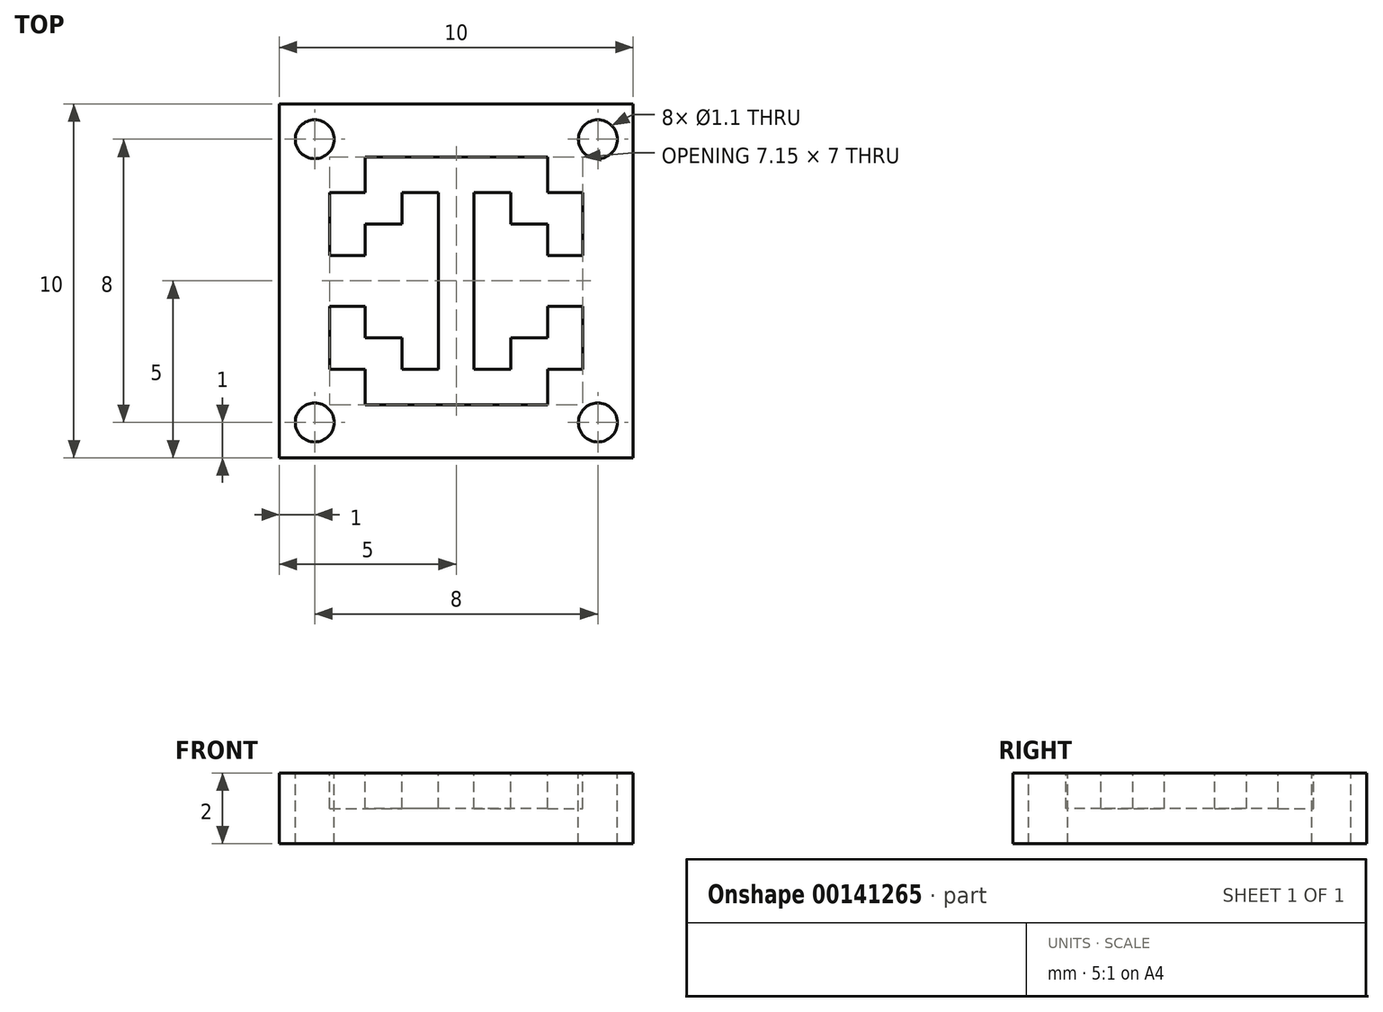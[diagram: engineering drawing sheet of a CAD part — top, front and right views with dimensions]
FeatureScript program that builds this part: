
annotation { "Feature Type Name" : "Feature", "Feature Type Description" : "" }
export const myFeature = defineFeature(function(context is Context, id is Id, definition is map)
    precondition{}
    {
        {
            var Q0;
            Q0=qCreatedBy(makeId("Top.planeOp"),FACE);
            var sketch = newSketch(context, id + "F0", { "sketchPlane" : qUnion([Q0])});
            skLineSegment(sketch, "E0.bottom", {"start": v(5, 5) * mm, "end": v(-5, 5) * mm});
            skLineSegment(sketch, "E0.top", {"start": v(5, -5) * mm, "end": v(-5, -5) * mm});
            skLineSegment(sketch, "E0.left", {"start": v(5, 5) * mm, "end": v(5, -5) * mm});
            skLineSegment(sketch, "E0.right", {"start": v(-5, 5) * mm, "end": v(-5, -5) * mm});
            skLineSegment(sketch, "E1.left", {"start": v(0.5, 0.5) * mm, "end": v(0.5, -0.5) * mm});
            skLineSegment(sketch, "E2", {"start": v(-0.5, 0.5) * mm, "end": v(-0.5, -0.5) * mm});
            skLineSegment(sketch, "E3", {"start": v(-0.5, -0.5) * mm, "end": v(-0.5, -2.5) * mm});
            skLineSegment(sketch, "E4", {"start": v(0.5, -0.5) * mm, "end": v(0.5, -2.5) * mm});
            skLineSegment(sketch, "E5", {"start": v(-0.5, -3.5) * mm, "end": v(-2.58, -3.5) * mm});
            skLineSegment(sketch, "E6", {"start": v(-0.5, -2.5) * mm, "end": v(-1.54, -2.5) * mm});
            skLineSegment(sketch, "E7", {"start": v(-3.58, -2.5) * mm, "end": v(-3.58, -0.71) * mm});
            skLineSegment(sketch, "E8", {"start": v(-3.58, -0.71) * mm, "end": v(-2.58, -0.71) * mm});
            skLineSegment(sketch, "E9", {"start": v(-2.58, -0.71) * mm, "end": v(-2.58, -1.6) * mm});
            skLineSegment(sketch, "E10", {"start": v(-0.5, -3.5) * mm, "end": v(0.5, -3.5) * mm});
            skLineSegment(sketch, "E11.MirrorCS", {"start": v(-0.5, 3.5) * mm, "end": v(0.5, 3.5) * mm});
            skLineSegment(sketch, "E12.MirrorCS", {"start": v(0.5, 0.5) * mm, "end": v(0.5, 2.5) * mm});
            skLineSegment(sketch, "E13.MirrorCS", {"start": v(-0.5, 0.5) * mm, "end": v(-0.5, 2.5) * mm});
            skLineSegment(sketch, "E14", {"start": v(-5, 0) * mm, "end": v(5, 0) * mm, "construction": true});
            skLineSegment(sketch, "E15", {"start": v(0, 5) * mm, "end": v(0, -5) * mm, "construction": true});
            skPoint(sketch, "E15.endSnap0", {"position": v(0, 5) * mm});
            skCircle(sketch, "E16", {"center": v(-4, -4) * mm, "radius": 0.55 * mm});
            skCircle(sketch, "E17.MirrorC", {"center": v(4, -4) * mm, "radius": 0.55 * mm});
            skCircle(sketch, "E18.MirrorC", {"center": v(-4, 4) * mm, "radius": 0.55 * mm});
            skLineSegment(sketch, "E19", {"start": v(-1.54, -2.5) * mm, "end": v(-1.54, -1.6) * mm});
            skLineSegment(sketch, "E20", {"start": v(-2.58, -1.6) * mm, "end": v(-1.54, -1.6) * mm});
            skLineSegment(sketch, "E21", {"start": v(-2.58, -2.5) * mm, "end": v(-2.58, -3.5) * mm});
            skLineSegment(sketch, "E22", {"start": v(-2.58, -2.5) * mm, "end": v(-3.58, -2.5) * mm});
            skLineSegment(sketch, "E23.MirrorCS", {"start": v(0.5, -3.5) * mm, "end": v(2.58, -3.5) * mm});
            skLineSegment(sketch, "E24.MirrorCS", {"start": v(2.58, -2.5) * mm, "end": v(2.58, -3.5) * mm});
            skLineSegment(sketch, "E25.MirrorCS", {"start": v(2.58, -2.5) * mm, "end": v(3.58, -2.5) * mm});
            skLineSegment(sketch, "E26.MirrorCS", {"start": v(3.58, -2.5) * mm, "end": v(3.58, -0.71) * mm});
            skLineSegment(sketch, "E27.MirrorCS", {"start": v(3.58, -0.71) * mm, "end": v(2.58, -0.71) * mm});
            skLineSegment(sketch, "E28.MirrorCS", {"start": v(2.58, -0.71) * mm, "end": v(2.58, -1.6) * mm});
            skLineSegment(sketch, "E29.MirrorCS", {"start": v(2.58, -1.6) * mm, "end": v(1.54, -1.6) * mm});
            skLineSegment(sketch, "E30.MirrorCS", {"start": v(1.54, -2.5) * mm, "end": v(1.54, -1.6) * mm});
            skLineSegment(sketch, "E31.MirrorCS", {"start": v(0.5, -2.5) * mm, "end": v(1.54, -2.5) * mm});
            skCircle(sketch, "E32.MirrorC", {"center": v(4, 4) * mm, "radius": 0.55 * mm});
            skLineSegment(sketch, "E33.MirrorCS", {"start": v(-0.5, 2.5) * mm, "end": v(-1.54, 2.5) * mm});
            skLineSegment(sketch, "E34.MirrorCS", {"start": v(-1.54, 2.5) * mm, "end": v(-1.54, 1.6) * mm});
            skLineSegment(sketch, "E35.MirrorCS", {"start": v(-2.58, 1.6) * mm, "end": v(-1.54, 1.6) * mm});
            skLineSegment(sketch, "E36.MirrorCS", {"start": v(-2.58, 0.71) * mm, "end": v(-2.58, 1.6) * mm});
            skLineSegment(sketch, "E37.MirrorCS", {"start": v(-3.58, 0.71) * mm, "end": v(-2.58, 0.71) * mm});
            skLineSegment(sketch, "E38.MirrorCS", {"start": v(-3.58, 2.5) * mm, "end": v(-3.58, 0.71) * mm});
            skLineSegment(sketch, "E39.MirrorCS", {"start": v(-2.58, 2.5) * mm, "end": v(-3.58, 2.5) * mm});
            skLineSegment(sketch, "E40.MirrorCS", {"start": v(-2.58, 2.5) * mm, "end": v(-2.58, 3.5) * mm});
            skLineSegment(sketch, "E41.MirrorCS", {"start": v(-0.5, 3.5) * mm, "end": v(-2.58, 3.5) * mm});
            skLineSegment(sketch, "E42.MirrorCS", {"start": v(0.5, 3.5) * mm, "end": v(2.58, 3.5) * mm});
            skLineSegment(sketch, "E43.MirrorCS", {"start": v(2.58, 2.5) * mm, "end": v(2.58, 3.5) * mm});
            skLineSegment(sketch, "E44.MirrorCS", {"start": v(2.58, 2.5) * mm, "end": v(3.58, 2.5) * mm});
            skLineSegment(sketch, "E45.MirrorCS", {"start": v(3.58, 2.5) * mm, "end": v(3.58, 0.71) * mm});
            skLineSegment(sketch, "E46.MirrorCS", {"start": v(3.58, 0.71) * mm, "end": v(2.58, 0.71) * mm});
            skLineSegment(sketch, "E47.MirrorCS", {"start": v(2.58, 0.71) * mm, "end": v(2.58, 1.6) * mm});
            skLineSegment(sketch, "E48.MirrorCS", {"start": v(2.58, 1.6) * mm, "end": v(1.54, 1.6) * mm});
            skLineSegment(sketch, "E49.MirrorCS", {"start": v(1.54, 2.5) * mm, "end": v(1.54, 1.6) * mm});
            skLineSegment(sketch, "E50.MirrorCS", {"start": v(0.5, 2.5) * mm, "end": v(1.54, 2.5) * mm});
            skSolve(sketch);
        }
        {
            var Q0;
            Q0=makeQuery(id+"F0.imprint","IMPRINT",FACE,{"disambiguationData":[TD([[makeQuery(id+"F0.imprint","IMPRINT",EDGE,{"derivedFrom":sQuery(id+"F0.wireOp",EDGE,"E0.bottom")}),1.0]])]});
            var Q1;
            Q1=makeQuery(id+"F0.imprint","IMPRINT",FACE,{"disambiguationData":[TD([[makeQuery(id+"F0.imprint","IMPRINT",EDGE,{"derivedFrom":sQuery(id+"F0.wireOp",EDGE,"E1.left")}),-1.0]])]});
            extrude(context, id + "F1", {"entities" : qUnion([Q0, Q1]), "oppositeDirection" : true, "depth" : 2 * mm});
        }
        {
            var Q0;
            Q0=makeQuery(id+"F0.imprint","IMPRINT",FACE,{"disambiguationData":[TD([[makeQuery(id+"F0.imprint","IMPRINT",EDGE,{"derivedFrom":sQuery(id+"F0.wireOp",EDGE,"E1.left")}),-1.0]])]});
            extrude(context, id + "F2", {"entities" : qUnion([Q0]), "operationType" : NewBodyOperationType.REMOVE, "oppositeDirection" : true, "depth" : 1 * mm});
        }
    });
